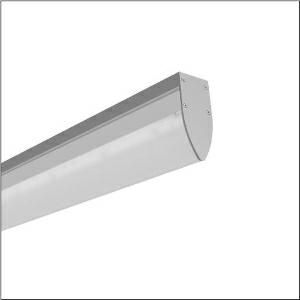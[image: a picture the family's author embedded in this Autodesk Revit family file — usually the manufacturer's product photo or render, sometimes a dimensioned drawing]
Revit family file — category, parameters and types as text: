
# Revit family: mira_r__21_td_51fr527d434a_4418
name_source: partatom
category: Lighting Fixtures
units: mm (PartAtom-declared; Revit-internal decimal feet)

## family parameters
Cut with Voids When Loaded = No
Host = Face
Light Source = No
Part Type = Normal
Room Calculation Point = No
Round Connector Dimension = Use Diameter
Shared = No

## types (1)
- Mira® 21 TD (1 x LED, 3660 lm, 26 W, 4000K)
    Apparent Load = 26 VA
    CIE Flux Codes = 40 68 87 81 100
    Color Rendering = 80
    Color Temperature = 4000K
    Default Elevation = 1800 mm
    Description = Mira® 21 TD, clean room luminaire, primary light control with reflector, primary optical cover: cover, of PMMA, frosted, light emission: direct distribution, primary light characteristic: symmetric, installation type: surface-mounted, LED, rated luminous flux: 3.660lm, luminous efficacy: 141lm/W, light colour: 840, colour temperature: 4000K, control gear: ON/OFF, with terminal, 3-pole, max. 2.5mm², mains connection: 230V, AC, 50/60Hz, rated input power: 26W, luminaire housing, of sheet steel, coated, pure white (RAL 9010), length: 600mm, width: 55mm, height: 120mm, protection rating (complete): IP43, insulation class (complete): insulation class I (protective earthing), certification: CE, UKCA, permissible operating ambient temperature: -5..+40°C, standard: EN 50419, packaging unit: 1 piece
    Height = 120 mm
    Lamp = 1 x LED
    Lamp Light Flux = 3660 lm
    Lamp Power = 26 W
    Lamp count = 1
    Length = 600 mm
    Luminous efficacy = 141 lm/W
    Manufacturer = Siteco
    ModVariant = No
    Model = 51FR527D434A
    Mounting Place = Ceiling
    Mounting Type = Surface mounted
    Number of Poles = 1
    OnlyDefault = Yes
    Power Factor = 1
    Product Name = Mira® 21 TD
    Product group = clean room luminaire | ceiling mounted
    ProductGroupID = 305
    Protection Class = Protection class I
    Protection Degree = IP 43
    RLX_Detail_Level = 1
    RLX_Emergency_Light_Flux = 0 lm
    RLX_Emergency_Type = 0
    RLX_Emergency_Type_DB = No
    RlxData = <blob elided: 25865 chars, md5=068a3915>
    Socket = socket
    Standby Power = 0 W
    System Light Flux = 3660 lm
    System Power = 26 W
    Type Comments = Product without accessories
    Type Image = l_1007115.jpg
    URL = http://relux.com
    VarID = ---
    Voltage = 0 V
    Weight = 0.00 kg
    Width = 55 mm

## geometry (parser evidence)
native form markers: Blend x4, Sweep x10
no freeform markers — native parametric forms only
